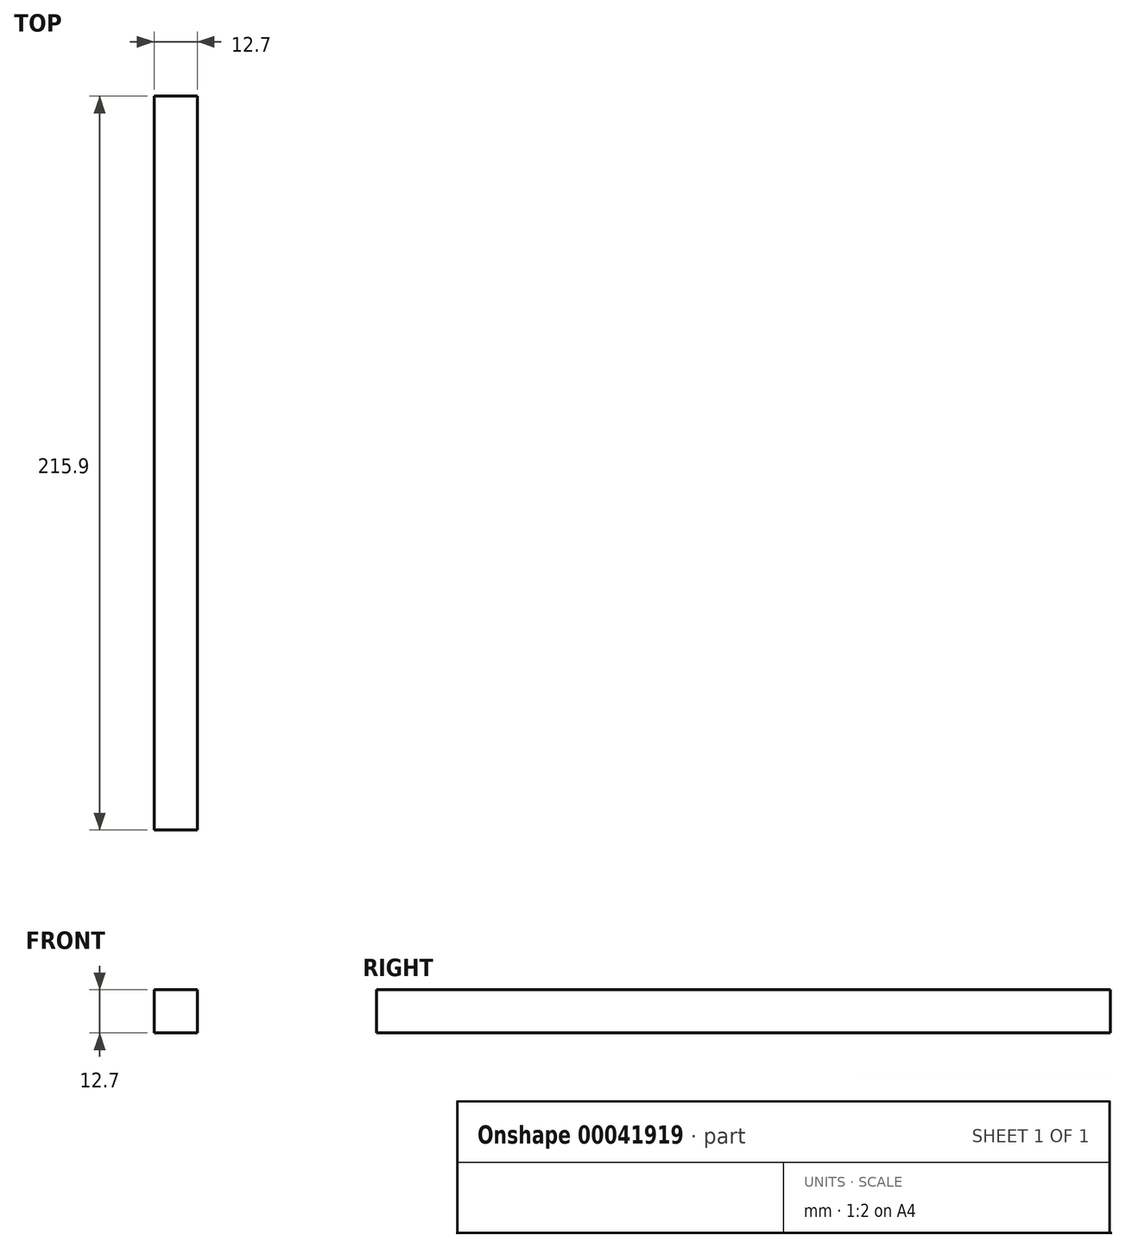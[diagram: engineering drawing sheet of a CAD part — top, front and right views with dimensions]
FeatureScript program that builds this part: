
annotation { "Feature Type Name" : "Feature", "Feature Type Description" : "" }
export const myFeature = defineFeature(function(context is Context, id is Id, definition is map)
    precondition{}
    {
        {
            var Q0;
            Q0=qCreatedBy(makeId("Front.planeOp"),FACE);
            var sketch = newSketch(context, id + "F0", { "sketchPlane" : qUnion([Q0])});
            skLineSegment(sketch, "E0.rect.bottom", {"start": v(6.35, 6.35) * mm, "end": v(-6.35, 6.35) * mm});
            skLineSegment(sketch, "E0.rect.top", {"start": v(6.35, -6.35) * mm, "end": v(-6.35, -6.35) * mm});
            skLineSegment(sketch, "E0.rect.left", {"start": v(6.35, 6.35) * mm, "end": v(6.35, -6.35) * mm});
            skLineSegment(sketch, "E0.rect.right", {"start": v(-6.35, 6.35) * mm, "end": v(-6.35, -6.35) * mm});
            skPoint(sketch, "E0.rect.middle", {"position": v(0, 0) * mm});
            skSolve(sketch);
        }
        {
            var Q0;
            Q0=makeQuery(id+"F0.imprint","IMPRINT",FACE,{"disambiguationData":[TD([[makeQuery(id+"F0.imprint","IMPRINT",EDGE,{"derivedFrom":sQuery(id+"F0.wireOp",EDGE,"E0.rect.bottom")}),1.0]])]});
            extrude(context, id + "F1", {"entities" : qUnion([Q0]), "endBound" : BoundingType.SYMMETRIC, "depth" : 215.9 * mm});
        }
    });
